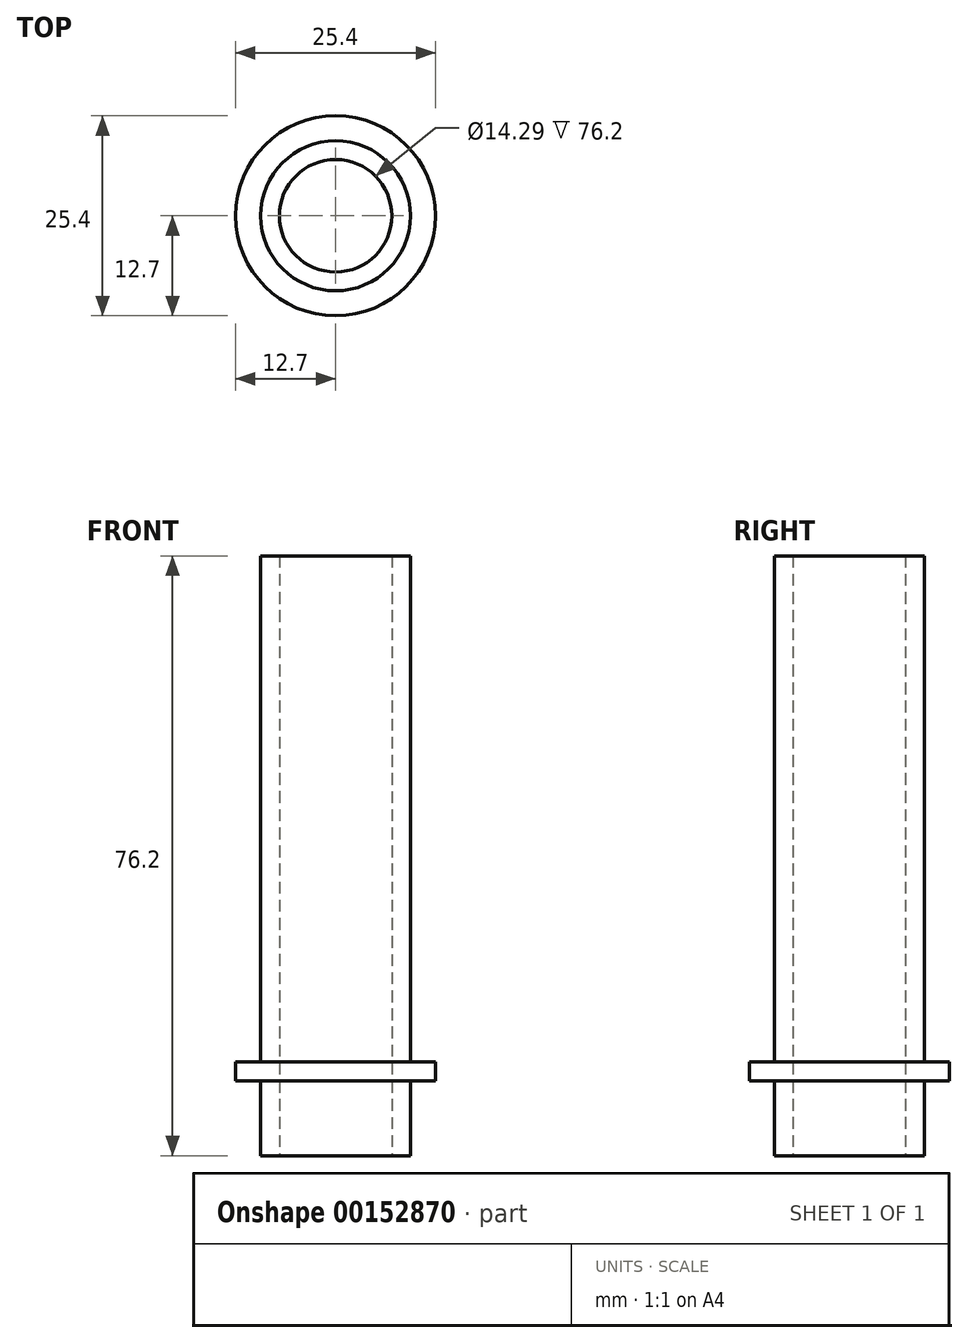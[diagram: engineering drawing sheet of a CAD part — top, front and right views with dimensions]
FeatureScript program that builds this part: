
annotation { "Feature Type Name" : "Feature", "Feature Type Description" : "" }
export const myFeature = defineFeature(function(context is Context, id is Id, definition is map)
    precondition{}
    {
        {
            var Q0;
            Q0=qCreatedBy(makeId("Top.planeOp"),FACE);
            var sketch = newSketch(context, id + "F0", { "sketchPlane" : qUnion([Q0])});
            skCircle(sketch, "E0", {"center": v(0, 0) * mm, "radius": 19.05 * mm});
            skCircle(sketch, "E1", {"center": v(0, 0) * mm, "radius": 7.14 * mm});
            skSolve(sketch);
        }
        {
            var Q0;
            Q0 = qSketchRegion(id + "F0", true);
            extrude(context, id + "F1", {"entities" : qUnion([Q0]), "depth" : 76.2 * mm});
        }
        {
            var Q0;
            Q0=qCreatedBy(makeId("Front.planeOp"),FACE);
            var sketch = newSketch(context, id + "F2", { "sketchPlane" : qUnion([Q0])});
            skLineSegment(sketch, "E2", {"start": v(0, 0) * mm, "end": v(9.53, 0) * mm, "construction": true});
            skLineSegment(sketch, "E3", {"start": v(9.53, 0) * mm, "end": v(9.53, 9.52) * mm});
            skLineSegment(sketch, "E4", {"start": v(9.53, 9.52) * mm, "end": v(12.7, 9.52) * mm});
            skLineSegment(sketch, "E5", {"start": v(12.7, 9.52) * mm, "end": v(12.7, 11.9) * mm});
            skLineSegment(sketch, "E6", {"start": v(12.7, 11.9) * mm, "end": v(9.53, 11.9) * mm});
            skLineSegment(sketch, "E7", {"start": v(9.53, 11.9) * mm, "end": v(9.53, 101.6) * mm});
            skLineSegment(sketch, "E8", {"start": v(9.53, 101.6) * mm, "end": v(34.92, 101.6) * mm});
            skLineSegment(sketch, "E9", {"start": v(34.92, 101.6) * mm, "end": v(34.92, 0) * mm});
            skLineSegment(sketch, "E10", {"start": v(34.92, 0) * mm, "end": v(9.53, 0) * mm});
            skSolve(sketch);
        }
        {
            var Q0;
            Q0=makeQuery(id+"F2.imprint","IMPRINT",FACE,{"disambiguationData":[TD([[makeQuery(id+"F2.imprint","IMPRINT",EDGE,{"derivedFrom":sQuery(id+"F2.wireOp",EDGE,"E3")}),-1.0]])]});
            var Q1;
            Q1=makeQuery(id+"F1.opExtrude","SWEPT_FACE",FACE,{"disambiguationData":[OSD([sQuery(id+"F0.wireOp",EDGE,"E0")])]});
            revolve(context, id + "F3", {"operationType" : NewBodyOperationType.REMOVE, "entities" : qUnion([Q0]), "axis" : qUnion([Q1]), "revolveType" : RevolveType.FULL, "oppositeDirection" : true});
        }
    });
